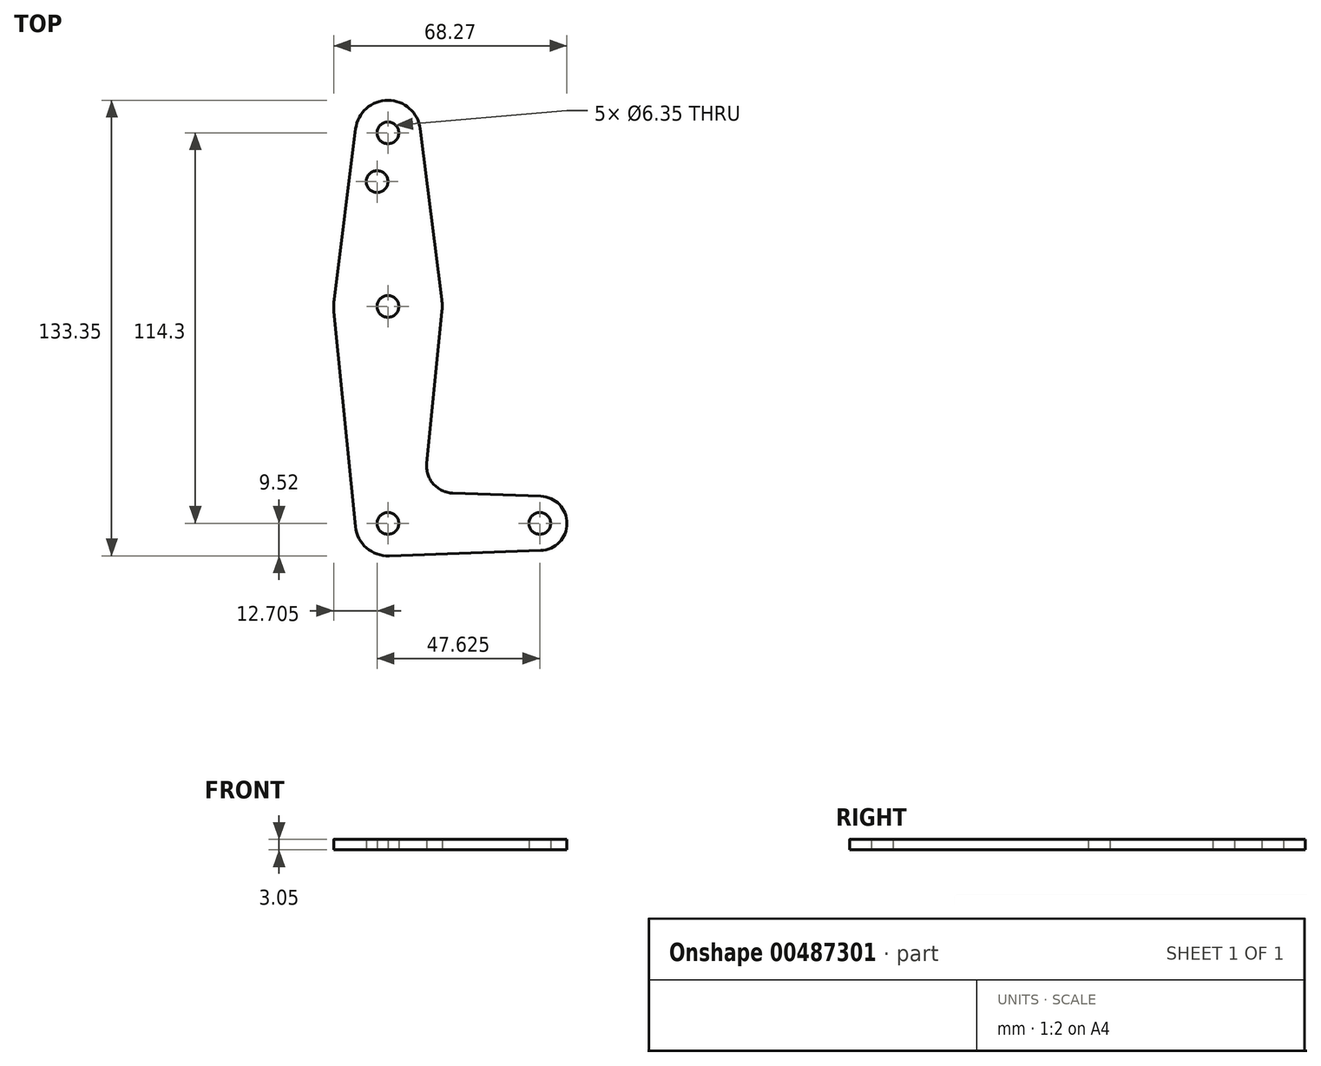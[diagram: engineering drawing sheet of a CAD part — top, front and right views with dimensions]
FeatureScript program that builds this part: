
annotation { "Feature Type Name" : "Feature", "Feature Type Description" : "" }
export const myFeature = defineFeature(function(context is Context, id is Id, definition is map)
    precondition{}
    {
        {
            var Q0;
            Q0=qCreatedBy(makeId("Top.planeOp"),FACE);
            var sketch = newSketch(context, id + "F0", { "sketchPlane" : qUnion([Q0])});
            skLineSegment(sketch, "E0", {"start": v(0, 0) * mm, "end": v(0, 114.3) * mm, "construction": true});
            skLineSegment(sketch, "E1", {"start": v(0, 0) * mm, "end": v(44.45, 0) * mm, "construction": true});
            skCircle(sketch, "E2", {"center": v(0, 114.3) * mm, "radius": 9.53 * mm});
            skCircle(sketch, "E3", {"center": v(0, 63.5) * mm, "radius": 15.88 * mm});
            skCircle(sketch, "E4", {"center": v(0, 0) * mm, "radius": 9.53 * mm});
            skCircle(sketch, "E5", {"center": v(44.45, 0) * mm, "radius": 7.94 * mm});
            skLineSegment(sketch, "E6", {"start": v(9.45, 115.5) * mm, "end": v(15.75, 65.48) * mm});
            skLineSegment(sketch, "E7", {"start": v(-9.45, 115.5) * mm, "end": v(-15.75, 65.48) * mm});
            skLineSegment(sketch, "E8", {"start": v(15.8, 61.91) * mm, "end": v(11.34, 17.6) * mm});
            skLineSegment(sketch, "E9", {"start": v(-15.8, 61.91) * mm, "end": v(-9.48, -0.95) * mm});
            skLineSegment(sketch, "E10", {"start": v(18.97, 8.85) * mm, "end": v(44.73, 7.93) * mm});
            skLineSegment(sketch, "E11", {"start": v(0.34, -9.52) * mm, "end": v(44.73, -7.93) * mm});
            skCircle(sketch, "E12", {"center": v(0, 63.5) * mm, "radius": 3.18 * mm});
            skCircle(sketch, "E13", {"center": v(0, 0) * mm, "radius": 3.18 * mm});
            skCircle(sketch, "E14", {"center": v(44.45, 0) * mm, "radius": 3.18 * mm});
            skCircle(sketch, "E15", {"center": v(0, 114.3) * mm, "radius": 3.18 * mm});
            skCircle(sketch, "E16", {"center": v(-3.18, 100.03) * mm, "radius": 3.18 * mm});
            skArc(sketch, "E17.filletArc", {"start": v(11.34, 17.6) * mm, "mid": v(13.26, 11.57) * mm, "end": v(18.97, 8.85) * mm});
            skSolve(sketch);
        }
        {
            var Q0;
            Q0 = qSketchRegion(id + "F0", true);
            extrude(context, id + "F1", {"entities" : qUnion([Q0]), "depth" : 3.05 * mm});
        }
    });
